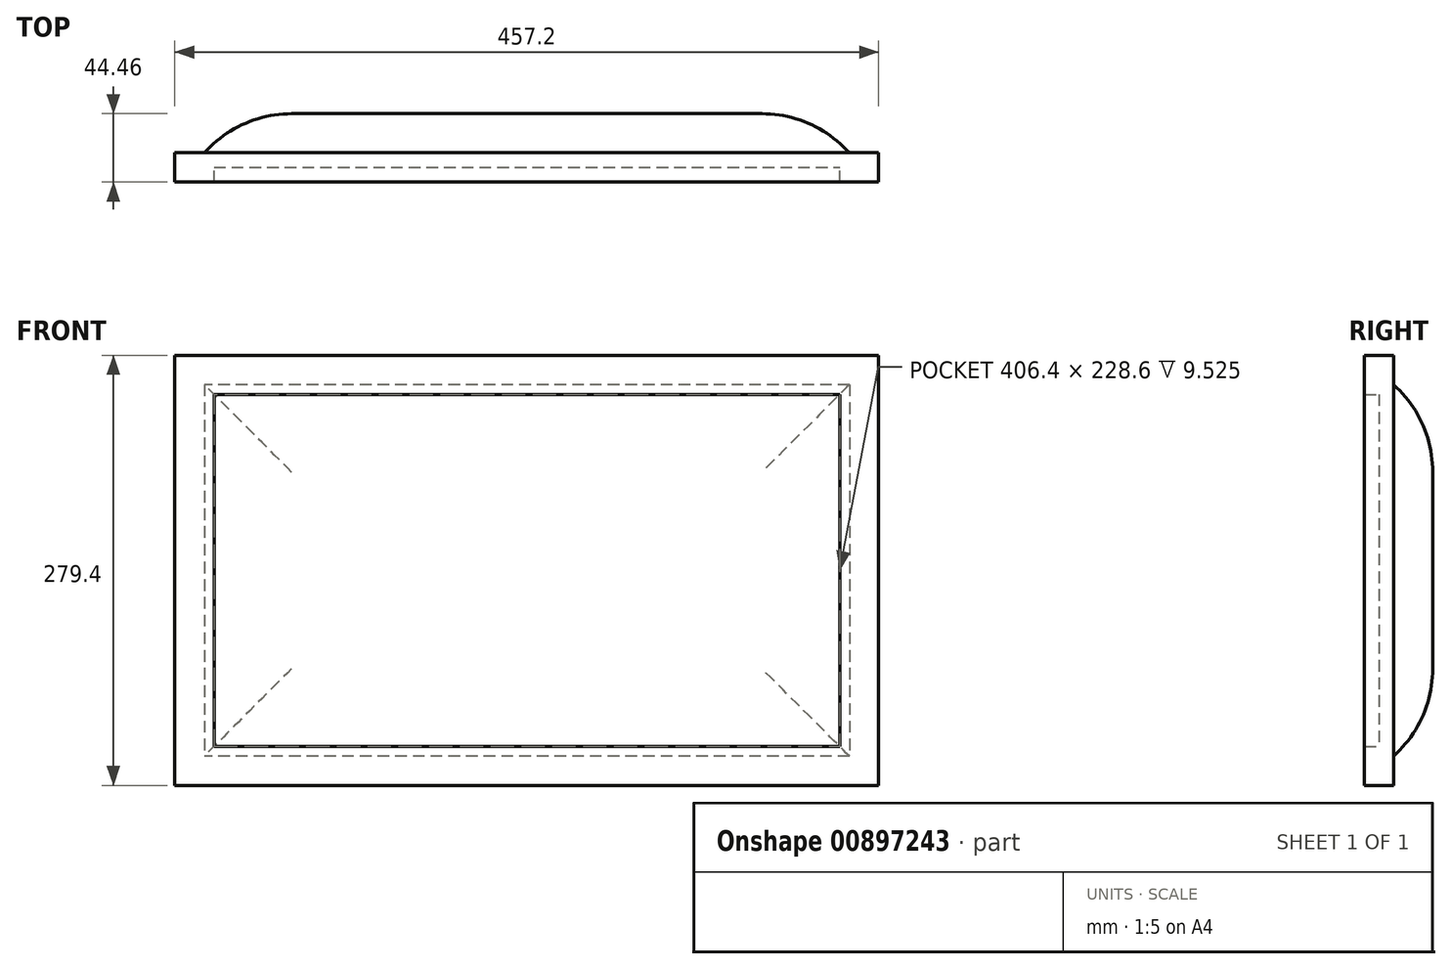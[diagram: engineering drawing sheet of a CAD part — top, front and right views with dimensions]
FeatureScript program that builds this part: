
annotation { "Feature Type Name" : "Feature", "Feature Type Description" : "" }
export const myFeature = defineFeature(function(context is Context, id is Id, definition is map)
    precondition{}
    {
        {
            var Q0;
            Q0=qCreatedBy(makeId("Front.planeOp"),FACE);
            var sketch = newSketch(context, id + "F0", { "sketchPlane" : qUnion([Q0])});
            skLineSegment(sketch, "E0.bottom", {"start": v(-203.2, 114.3) * mm, "end": v(203.2, 114.3) * mm});
            skLineSegment(sketch, "E0.top", {"start": v(-203.2, -114.3) * mm, "end": v(203.2, -114.3) * mm});
            skLineSegment(sketch, "E0.left", {"start": v(-203.2, 114.3) * mm, "end": v(-203.2, -114.3) * mm});
            skLineSegment(sketch, "E0.right", {"start": v(203.2, 114.3) * mm, "end": v(203.2, -114.3) * mm});
            skPoint(sketch, "E0.middle", {"position": v(0, 0) * mm});
            skSolve(sketch);
        }
        {
            var Q0;
            Q0=makeQuery(id+"F0.imprint","IMPRINT",FACE,{"disambiguationData":[TD([[makeQuery(id+"F0.imprint","IMPRINT",EDGE,{"derivedFrom":sQuery(id+"F0.wireOp",EDGE,"E0.bottom")}),-1.0]])]});
            extrude(context, id + "F1", {"entities" : qUnion([Q0]), "depth" : 12.7 * mm, "offsetDistance" : 25.4 * mm});
        }
        {
            var Q0;
            Q0=makeQuery(id+"F1.opExtrude","CAP_FACE",FACE,{"disambiguationData":[OSD([sQuery(id+"F0.wireOp",EDGE,"E0.bottom"),sQuery(id+"F0.wireOp",EDGE,"E0.top"),sQuery(id+"F0.wireOp",EDGE,"E0.left"),sQuery(id+"F0.wireOp",EDGE,"E0.right")])],"isStart":false});
            var sketch = newSketch(context, id + "F2", { "sketchPlane" : qUnion([Q0])});
            skLineSegment(sketch, "E1.0", {"start": v(-228.6, 139.7) * mm, "end": v(-228.6, -139.7) * mm});
            skLineSegment(sketch, "E1.1", {"start": v(-228.6, 139.7) * mm, "end": v(228.6, 139.7) * mm});
            skLineSegment(sketch, "E1.2", {"start": v(228.6, 139.7) * mm, "end": v(228.6, -139.7) * mm});
            skLineSegment(sketch, "E1.3", {"start": v(-228.6, -139.7) * mm, "end": v(228.6, -139.7) * mm});
            skLineSegment(sketch, "E2.0", {"start": v(-203.2, 114.3) * mm, "end": v(-203.2, -114.3) * mm});
            skLineSegment(sketch, "E3.0", {"start": v(-203.2, 114.3) * mm, "end": v(203.2, 114.3) * mm});
            skLineSegment(sketch, "E4.0", {"start": v(-203.2, -114.3) * mm, "end": v(203.2, -114.3) * mm});
            skLineSegment(sketch, "E5.0", {"start": v(203.2, 114.3) * mm, "end": v(203.2, -114.3) * mm});
            skSolve(sketch);
        }
        {
            var Q0;
            Q0=qSketchRegion(id+"F2",true);
            extrude(context, id + "F3", {"entities" : qUnion([Q0]), "endBound" : BoundingType.SYMMETRIC, "depth" : 19.05 * mm, "offsetDistance" : 25.4 * mm});
        }
        {
            var Q0;
            Q0=makeQuery(id+"F3.opExtrude","CAP_FACE",FACE,{"disambiguationData":[OSD([sQuery(id+"F2.wireOp",EDGE,"E1.0"),sQuery(id+"F2.wireOp",EDGE,"E1.1"),sQuery(id+"F2.wireOp",EDGE,"E1.2"),sQuery(id+"F2.wireOp",EDGE,"E1.3"),sQuery(id+"F2.wireOp",EDGE,"E2.0"),sQuery(id+"F2.wireOp",EDGE,"E3.0"),sQuery(id+"F2.wireOp",EDGE,"E4.0"),sQuery(id+"F2.wireOp",EDGE,"E5.0")])],"isStart":true});
            var sketch = newSketch(context, id + "F4", { "sketchPlane" : qUnion([Q0])});
            skLineSegment(sketch, "E6.bottom", {"start": v(-209.55, 120.65) * mm, "end": v(209.55, 120.65) * mm});
            skLineSegment(sketch, "E6.top", {"start": v(-209.55, -120.65) * mm, "end": v(209.55, -120.65) * mm});
            skLineSegment(sketch, "E6.left", {"start": v(-209.55, 120.65) * mm, "end": v(-209.55, -120.65) * mm});
            skLineSegment(sketch, "E6.right", {"start": v(209.55, 120.65) * mm, "end": v(209.55, -120.65) * mm});
            skPoint(sketch, "E6.middle", {"position": v(0, 0) * mm});
            skSolve(sketch);
        }
        {
            var Q0;
            Q0=qSketchRegion(id+"F4",true);
            extrude(context, id + "F5", {"entities" : qUnion([Q0]), "operationType" : NewBodyOperationType.ADD, "depth" : 25.4 * mm, "offsetDistance" : 25.4 * mm});
        }
        {
            var Q0;
            Q0=makeQuery(id+"F5.opExtrude","CAP_EDGE",EDGE,{"disambiguationData":[OSD([sQuery(id+"F4.wireOp",EDGE,"E6.left")])],"isStart":false});
            var Q1;
            Q1=makeQuery(id+"F5.opExtrude","CAP_EDGE",EDGE,{"disambiguationData":[OSD([sQuery(id+"F4.wireOp",EDGE,"E6.bottom")])],"isStart":false});
            var Q2;
            Q2=makeQuery(id+"F5.opExtrude","CAP_EDGE",EDGE,{"disambiguationData":[OSD([sQuery(id+"F4.wireOp",EDGE,"E6.right")])],"isStart":false});
            var Q3;
            Q3=makeQuery(id+"F5.opExtrude","CAP_EDGE",EDGE,{"disambiguationData":[OSD([sQuery(id+"F4.wireOp",EDGE,"E6.top")])],"isStart":false});
            fillet(context, id + "F6", {"entities" : qUnion([Q0, Q1, Q2, Q3]), "radius" : 76.2 * mm, "tangentPropagation" : true, "allowEdgeOverflow" : false});
        }
    });
